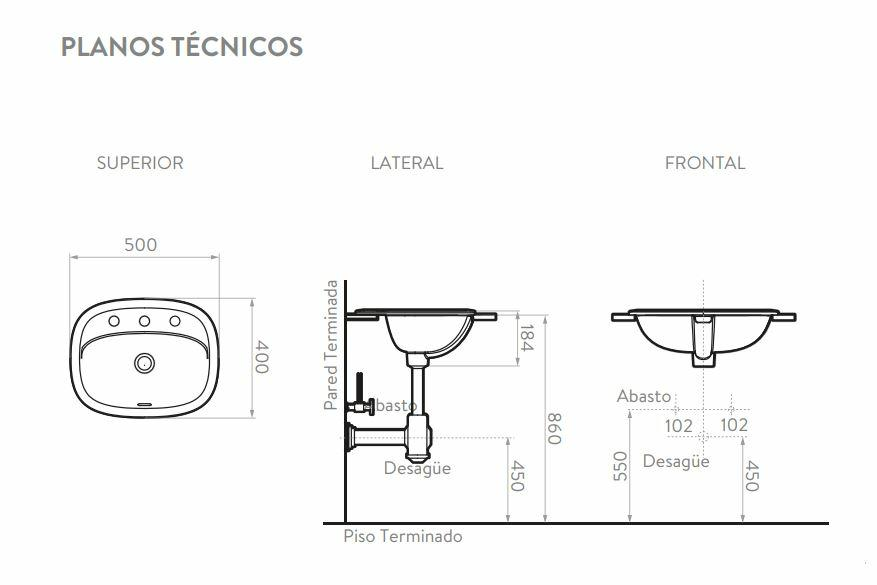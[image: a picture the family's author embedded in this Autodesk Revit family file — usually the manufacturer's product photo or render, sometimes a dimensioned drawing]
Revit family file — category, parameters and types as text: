
# Revit family: O14091001-CASCADE SOBREPONER
name_source: partatom
category: Generic Models
units: mm (PartAtom-declared; Revit-internal decimal feet)

## family parameters
Can host rebar = No
Cut with Voids When Loaded = No
Host = Face
OmniClass Number = 23.45.05.14.14
OmniClass Title = Sinks/Lavatories
Part Type = Normal
Room Calculation Point = No
Round Connector Dimension = Use Diameter
Shared = No

## types (1)
- O14091001-CASCADE SOBREPONER
    Alto = 184 mm  [stored 0.603675 ft]
    Altura de instalación Según Norma = 34” (864 cm)
    Ancho = 500 mm
    Creado por = IDD
    Default Elevation = 1219 mm
    Dimensiones generales producto (H * W * D) = 7,2” x 15,7” x 19,6” (18,4 cm x 40 cm x 50 cm)
    Fabricante = Corona
    Fecha de creación = 29/07/2020
    Garantía = De por vida
    Material = Corona_Cerámica_Sinterizada
    Peso Bruto aprox = 16,9 Lb (7,7 kg)
    Peso Neto aprox = 15,6 Lb (7,1 kg)
    Profundidad = 400 mm  [stored 1.31234 ft]
    Referencia = O14091001

note: [stored X ft] marks values corroborated as IEEE doubles in the binary element streams (Revit-internal decimal feet)

## geometry (parser evidence)
native form markers: Sweep x6
no freeform markers — native parametric forms only
